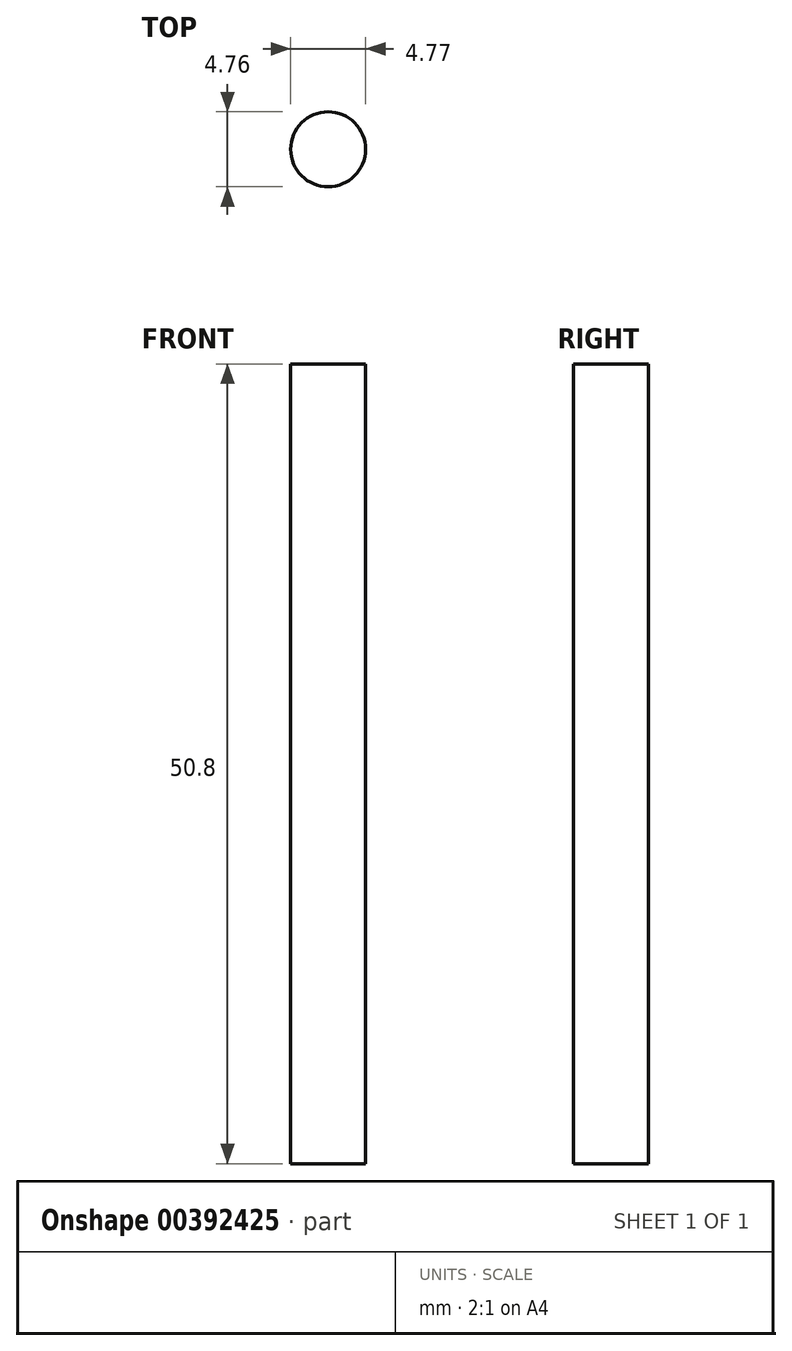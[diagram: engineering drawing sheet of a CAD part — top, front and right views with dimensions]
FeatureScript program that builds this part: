
annotation { "Feature Type Name" : "Feature", "Feature Type Description" : "" }
export const myFeature = defineFeature(function(context is Context, id is Id, definition is map)
    precondition{}
    {
        {
            var Q0;
            Q0=qCreatedBy(makeId("Top.planeOp"),FACE);
            var sketch = newSketch(context, id + "F0", { "sketchPlane" : qUnion([Q0])});
            skCircle(sketch, "E0", {"center": v(-100.55, -29) * mm, "radius": 2.38 * mm});
            skSolve(sketch);
        }
        {
            var Q0;
            Q0=makeQuery(id+"F0.imprint","IMPRINT",FACE,{"disambiguationData":[TD([[makeQuery(id+"F0.imprint","IMPRINT",EDGE,{"derivedFrom":sQuery(id+"F0.wireOp",EDGE,"E0")}),1.0]])]});
            extrude(context, id + "F1", {"entities" : qUnion([Q0]), "depth" : 50.8 * mm});
        }
    });
